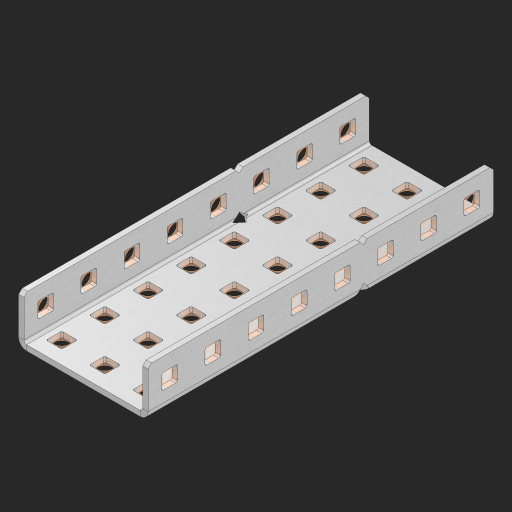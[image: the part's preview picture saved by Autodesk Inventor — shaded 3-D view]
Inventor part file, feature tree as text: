
AUTODESK INVENTOR PART (.ipt)
format: ipt  version: 2023 (Build 270158000, 158)  size: 821,248 bytes
history: native  units: in
note: dims shown in document units (in); Inventor stores cm internally (conversion verified against a paired STEP export)
features: other x45, extrude x39, sheet_metal_op x10, sketch x8, mirror x1, pattern_linear x1, chamfer x1
ambient origin geometry x8: Origin, YZ Plane, XZ Plane, XY Plane, X Axis, Y Axis, Z Axis, Center Point
bodies: Solid1 (feature_tree), Body (feature_tree)
feature tree (105):
  other  "Flange Pattern Plane"
  sheet_metal_op  "Flange Pattern"
  sheet_metal_op  "Body Pattern"
  other  "Arc Length"
  mirror  "Notch Mirror"
  pattern_linear  "Notch Pattern"  Spacing1=0.25in  [1 undecoded]
  chamfer  "End Chamfer"
  extrude  "Half Cut"  Depth=0.0625in
  sketch  "Sketch1"  dims[d0=1.5in]
  other  "Plate1"
  sketch  "Sketch2"  dims[d1=4.0in]
  other  "Plate2"
  sheet_metal_op  "Bend1"
  sheet_metal_op  "Corner1"
  sketch  "Sketch3"  dims[d2=0.0625in]
  other  "Flange Pattern Sketch"
  sketch  "Sketch7"  dims[d3=0.0625in]
  other  "Srf1"
  other  "Srf2"
  sketch  "Sketch8"  dims[d4=0.0312in]
  sketch  "Sketch9"  dims[d5=0.125in]
  other  "Srf91"
  sheet_metal_op  "Body Pattern Sketch"
  other  "Srf92"
  sketch  "Sketch13"  dims[d6=0.0625in]
  sketch  "Sketch14"  dims[d7=0.5in d8=90.0deg d9=0.0312in d10=0.25in d11=0.0625in d12=0.0625in d16=0.182in d17=0.02in d18=0.0625in d19=0.0in d20=0.25in d21=0.25in d46=0.172in d47=1.0in d48=0.0in d49=0.182in d50=0.02in d51=0.25in d52=0.25in d53=0.0625in d54=0.0in d55=0.172in d56=1.0in d57=0.0in d60=3.1496in d62=0.5in d63=1.1811in d65=0.5in d85=0.1473in d86=0.1782in d88=0.04in d89=0.0625in d90=0.0in d91=0.04in d92=0.0491in d95=2.5in d96=0.04in d97=0.25in d98=45.0deg d101=0.0in d102=2.497in d131=1.5in d132=3.1496in d134=0.5in d139=0.5in]
  other  "Srf856"
  other  "Srf1310"
  other  "Srf1311"
  other  "Srf1312"
  other  "Srf1376"
  other  "Srf1377"
  other  "Srf1728"
  other  "Srf1755"
  other  "Srf1878"
  other  "Srf1879"
  other  "Srf1880"
  other  "Srf1881"
  other  "Srf1882"
  other  "Srf1883"
  other  "Srf1884"
  other  "Srf1885"
  other  "Srf1886"
  other  "Srf1887"
  other  "Srf1942"
  other  "Srf1943"
  other  "Srf1944"
  other  "Srf1945"
  other  "Srf1946"
  other  "Srf1947"
  other  "Srf1948"
  other  "Srf1949"
  other  "Srf1950"
  other  "Srf1951"
  other  "Srf1952"
  other  "Srf1953"
  other  "Srf1954"
  other  "Srf1955"
  other  "Srf1956"
  other  "Srf1957"
  other  "Srf1958"
  other  "Srf1959"
  sheet_metal_op  "Flange Stamp"
  sheet_metal_op  "Flange Circle"
  sheet_metal_op  "Body Stamp"
  sheet_metal_op  "Body Circle"
  sheet_metal_op  "Notch"
  extrude  "ExtrusionSrf2"  Depth=0.0625in
  extrude  "ExtrusionSrf92"  Depth=1.5in
  extrude  "ExtrusionSrf856"  Depth=0.02in
  extrude  "ExtrusionSrf1310"  Depth=0.0625in
  extrude  "ExtrusionSrf1311"  TaperAngle=0.0deg  [1 undecoded]
  extrude  "ExtrusionSrf1312"  Depth=0.25in
  extrude  "ExtrusionSrf1376"  Depth=0.25in
  extrude  "ExtrusionSrf1377"  Depth=1.5in
  extrude  "ExtrusionSrf1728"  Depth=1.5in TaperAngle=0.0deg
  extrude  "ExtrusionSrf1755"  Depth=1.5in
  extrude  "ExtrusionSrf1878"  Depth=0.02in
  extrude  "ExtrusionSrf1879"  Depth=0.25in
  extrude  "ExtrusionSrf1880"  Depth=0.25in
  extrude  "ExtrusionSrf1881"  Depth=0.0625in
  extrude  "ExtrusionSrf1882"  TaperAngle=0.0deg  [1 undecoded]
  extrude  "ExtrusionSrf1883"  Depth=1.5in
  extrude  "ExtrusionSrf1884"  Depth=1.5in TaperAngle=0.0deg
  extrude  "ExtrusionSrf1885"  Depth=1.5in
  extrude  "ExtrusionSrf1886"  Depth=1.5in
  extrude  "ExtrusionSrf1887"  Depth=1.5in
  extrude  "ExtrusionSrf1942"  Depth=1.5in
  extrude  "ExtrusionSrf1943"  Depth=1.5in
  extrude  "ExtrusionSrf1944"  Depth=0.0625in
  extrude  "ExtrusionSrf1945"  TaperAngle=0.0deg  [1 undecoded]
  extrude  "ExtrusionSrf1946"  Depth=1.5in
  extrude  "ExtrusionSrf1947"  Depth=1.5in
  extrude  "ExtrusionSrf1948"  Depth=1.5in
  extrude  "ExtrusionSrf1949"  Depth=0.25in TaperAngle=45.0deg
  extrude  "ExtrusionSrf1950"  TaperAngle=0.0deg  [1 undecoded]
  extrude  "ExtrusionSrf1951"  Depth=1.5in
  extrude  "ExtrusionSrf1952"  Depth=1.5in
  extrude  "ExtrusionSrf1953"  Depth=1.5in
  extrude  "ExtrusionSrf1954"  Depth=1.5in
  extrude  "ExtrusionSrf1955"  Depth=1.5in
  extrude  "ExtrusionSrf1956"  [1 undecoded]
  extrude  "ExtrusionSrf1957"  [1 undecoded]
  extrude  "ExtrusionSrf1958"  [1 undecoded]
  extrude  "ExtrusionSrf1959"  [1 undecoded]
note: 9 required parameter values undecoded (feature->parameter linkage not recoverable at this tier; creation-order binding heuristic only, values carry confidence <= 0.55)
